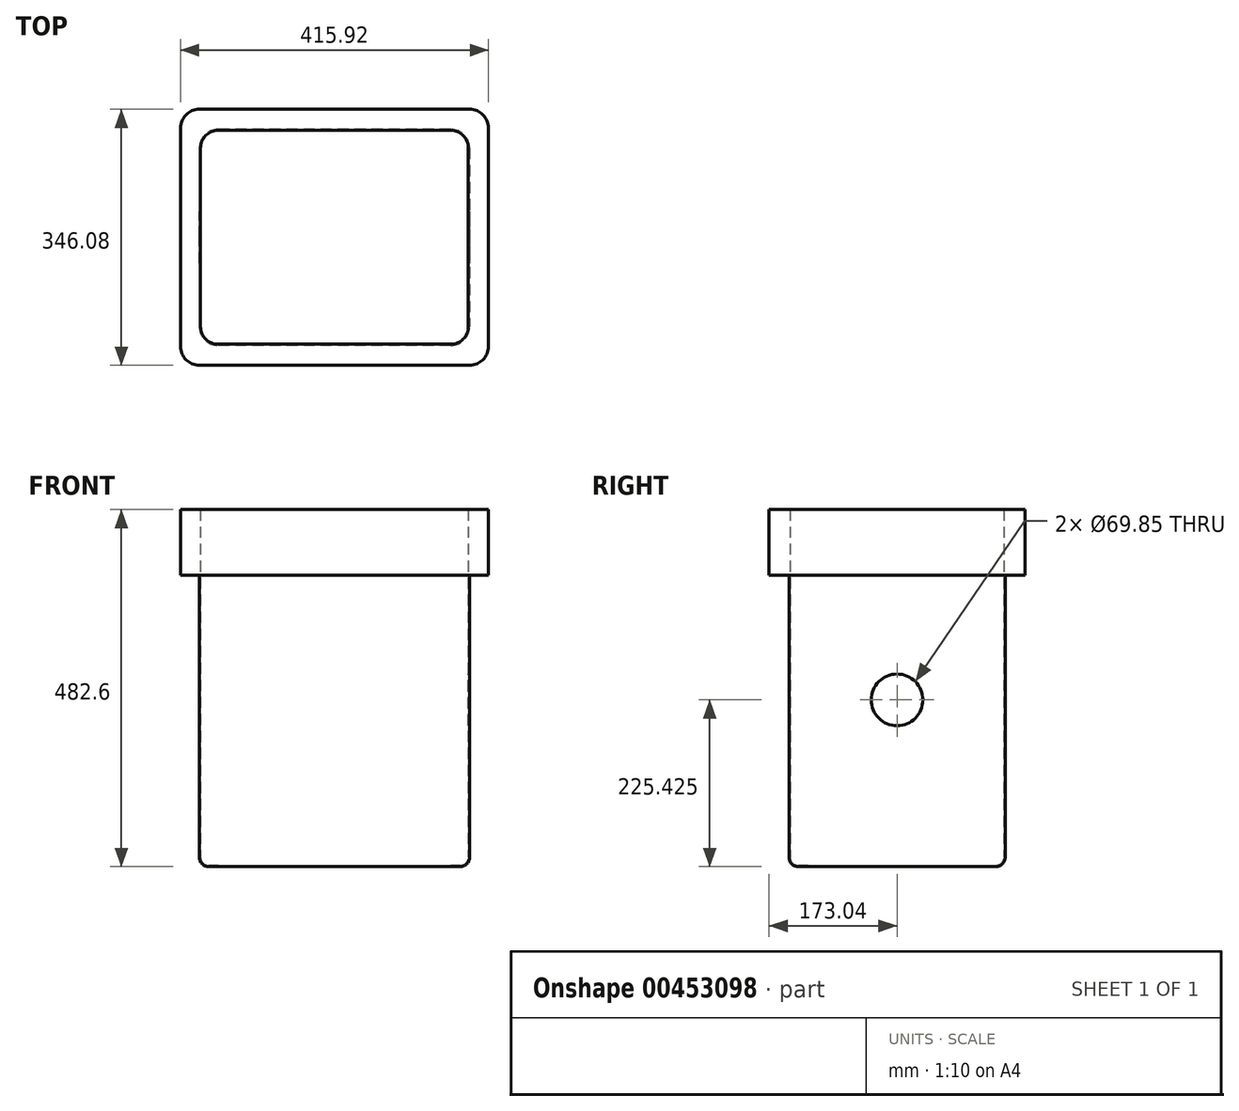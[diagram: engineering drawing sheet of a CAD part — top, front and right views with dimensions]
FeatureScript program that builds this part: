
annotation { "Feature Type Name" : "Feature", "Feature Type Description" : "" }
export const myFeature = defineFeature(function(context is Context, id is Id, definition is map)
    precondition{}
    {
        {
            var Q0;
            Q0=qCreatedBy(makeId("Top.planeOp"),FACE);
            var sketch = newSketch(context, id + "F0", { "sketchPlane" : qUnion([Q0])});
            skLineSegment(sketch, "E0.bottom", {"start": v(182.56, 146.05) * mm, "end": v(-182.56, 146.05) * mm});
            skLineSegment(sketch, "E0.top", {"start": v(182.56, -146.05) * mm, "end": v(-182.56, -146.05) * mm});
            skLineSegment(sketch, "E0.left", {"start": v(182.56, 146.05) * mm, "end": v(182.56, -146.05) * mm});
            skLineSegment(sketch, "E0.right", {"start": v(-182.56, 146.05) * mm, "end": v(-182.56, -146.05) * mm});
            skPoint(sketch, "E0.middle", {"position": v(0, 0) * mm});
            skSolve(sketch);
        }
        {
            var Q0;
            Q0=qSketchRegion(id+"F0",true);
            extrude(context, id + "F1", {"entities" : qUnion([Q0]), "offsetDistance" : 25.4 * mm, "depth" : 482.6 * mm});
        }
        {
            var Q0;
            Q0=makeQuery(id+"F1.opExtrude","SWEPT_EDGE",EDGE,{"disambiguationData":[OSD([sQuery(id+"F0.wireOp",EDGE,"E0.top"),sQuery(id+"F0.wireOp",EDGE,"E0.right")])]});
            var Q1;
            Q1=makeQuery(id+"F1.opExtrude","SWEPT_EDGE",EDGE,{"disambiguationData":[OSD([sQuery(id+"F0.wireOp",EDGE,"E0.top"),sQuery(id+"F0.wireOp",EDGE,"E0.left")])]});
            var Q2;
            Q2=makeQuery(id+"F1.opExtrude","SWEPT_EDGE",EDGE,{"disambiguationData":[OSD([sQuery(id+"F0.wireOp",EDGE,"E0.bottom"),sQuery(id+"F0.wireOp",EDGE,"E0.left")])]});
            var Q3;
            Q3=makeQuery(id+"F1.opExtrude","SWEPT_EDGE",EDGE,{"disambiguationData":[OSD([sQuery(id+"F0.wireOp",EDGE,"E0.bottom"),sQuery(id+"F0.wireOp",EDGE,"E0.right")])]});
            fillet(context, id + "F2", {"entities" : qUnion([Q0, Q1, Q2, Q3]), "radius" : 25.4 * mm, "tangentPropagation" : true, "allowEdgeOverflow" : false});
        }
        {
            var Q0;
            Q0=makeQuery(id+"F1.opExtrude","CAP_EDGE",EDGE,{"disambiguationData":[OSD([sQuery(id+"F0.wireOp",EDGE,"E0.top")])],"isStart":true});
            fillet(context, id + "F3", {"entities" : qUnion([Q0]), "radius" : 12.7 * mm, "tangentPropagation" : true, "allowEdgeOverflow" : false});
        }
        {
            var Q0;
            Q0=makeQuery(id+"F1.opExtrude","CAP_FACE",FACE,{"disambiguationData":[OSD([sQuery(id+"F0.wireOp",EDGE,"E0.bottom"),sQuery(id+"F0.wireOp",EDGE,"E0.top"),sQuery(id+"F0.wireOp",EDGE,"E0.left"),sQuery(id+"F0.wireOp",EDGE,"E0.right")])],"isStart":false});
            shell(context, id + "F4", {"entities" : qUnion([Q0]), "thickness" : 1.59 * mm});
        }
        {
            var Q0;
            Q0=makeQuery(id+"F1.opExtrude","SWEPT_FACE",FACE,{"disambiguationData":[OSD([sQuery(id+"F0.wireOp",EDGE,"E0.left")])]});
            var sketch = newSketch(context, id + "F5", { "sketchPlane" : qUnion([Q0])});
            skLineSegment(sketch, "E1", {"start": v(0, 12.7) * mm, "end": v(0, 482.6) * mm, "construction": true});
            skCircle(sketch, "E2", {"center": v(0, 225.42) * mm, "radius": 34.93 * mm});
            skPoint(sketch, "E3", {"position": v(0, 260.35) * mm});
            skSolve(sketch);
        }
        {
            var Q0;
            Q0=qSketchRegion(id+"F5",true);
            extrude(context, id + "F6", {"entities" : qUnion([Q0]), "operationType" : NewBodyOperationType.REMOVE, "endBound" : BoundingType.THROUGH_ALL, "oppositeDirection" : true, "depth" : 25.4 * mm, "offsetDistance" : 25.4 * mm});
        }
        {
            var Q0;
            Q0=makeQuery(id+"F1.opExtrude","CAP_FACE",FACE,{"disambiguationData":[OSD([sQuery(id+"F0.wireOp",EDGE,"E0.bottom"),sQuery(id+"F0.wireOp",EDGE,"E0.top"),sQuery(id+"F0.wireOp",EDGE,"E0.left"),sQuery(id+"F0.wireOp",EDGE,"E0.right")])],"isStart":false});
            var sketch = newSketch(context, id + "F7", { "sketchPlane" : qUnion([Q0])});
            skLineSegment(sketch, "E4.bottom", {"start": v(207.96, 173.04) * mm, "end": v(-207.96, 173.04) * mm});
            skLineSegment(sketch, "E4.top", {"start": v(207.96, -173.04) * mm, "end": v(-207.96, -173.04) * mm});
            skLineSegment(sketch, "E4.left", {"start": v(207.96, 173.04) * mm, "end": v(207.96, -173.04) * mm});
            skLineSegment(sketch, "E4.right", {"start": v(-207.96, 173.04) * mm, "end": v(-207.96, -173.04) * mm});
            skPoint(sketch, "E4.middle", {"position": v(0, 0) * mm});
            skLineSegment(sketch, "E5", {"start": v(-182.56, 120.65) * mm, "end": v(-182.56, -120.65) * mm});
            skLineSegment(sketch, "E6", {"start": v(-157.16, -146.05) * mm, "end": v(157.16, -146.05) * mm});
            skLineSegment(sketch, "E7", {"start": v(182.56, -120.65) * mm, "end": v(182.56, 120.65) * mm});
            skLineSegment(sketch, "E8", {"start": v(157.16, 146.05) * mm, "end": v(-157.16, 146.05) * mm});
            skArc(sketch, "E9", {"start": v(-157.16, 146.05) * mm, "mid": v(-175.12, 138.61) * mm, "end": v(-182.56, 120.65) * mm});
            skArc(sketch, "E10", {"start": v(-182.56, -120.65) * mm, "mid": v(-175.12, -138.61) * mm, "end": v(-157.16, -146.05) * mm});
            skArc(sketch, "E11", {"start": v(157.16, -146.05) * mm, "mid": v(175.12, -138.61) * mm, "end": v(182.56, -120.65) * mm});
            skArc(sketch, "E12", {"start": v(182.56, 120.65) * mm, "mid": v(175.12, 138.61) * mm, "end": v(157.16, 146.05) * mm});
            skSolve(sketch);
        }
        {
            var Q0;
            Q0=qSketchRegion(id+"F7",true);
            extrude(context, id + "F8", {"entities" : qUnion([Q0]), "operationType" : NewBodyOperationType.ADD, "oppositeDirection" : true, "depth" : 88.9 * mm, "offsetDistance" : 25.4 * mm});
        }
        {
            var Q0;
            Q0=makeQuery(id+"F8.opExtrude","SWEPT_EDGE",EDGE,{"disambiguationData":[OSD([sQuery(id+"F7.wireOp",EDGE,"E4.top"),sQuery(id+"F7.wireOp",EDGE,"E4.right")])]});
            var Q1;
            Q1=makeQuery(id+"F8.opExtrude","SWEPT_EDGE",EDGE,{"disambiguationData":[OSD([sQuery(id+"F7.wireOp",EDGE,"E4.top"),sQuery(id+"F7.wireOp",EDGE,"E4.left")])]});
            var Q2;
            Q2=makeQuery(id+"F8.opExtrude","SWEPT_EDGE",EDGE,{"disambiguationData":[OSD([sQuery(id+"F7.wireOp",EDGE,"E4.bottom"),sQuery(id+"F7.wireOp",EDGE,"E4.left")])]});
            var Q3;
            Q3=makeQuery(id+"F8.opExtrude","SWEPT_EDGE",EDGE,{"disambiguationData":[OSD([sQuery(id+"F7.wireOp",EDGE,"E4.bottom"),sQuery(id+"F7.wireOp",EDGE,"E4.right")])]});
            fillet(context, id + "F9", {"entities" : qUnion([Q0, Q1, Q2, Q3]), "tangentPropagation" : true, "radius" : 25.4 * mm, "defaultsChanged" : true, "vertexSettings" : [], "allowEdgeOverflow" : false});
        }
    });
